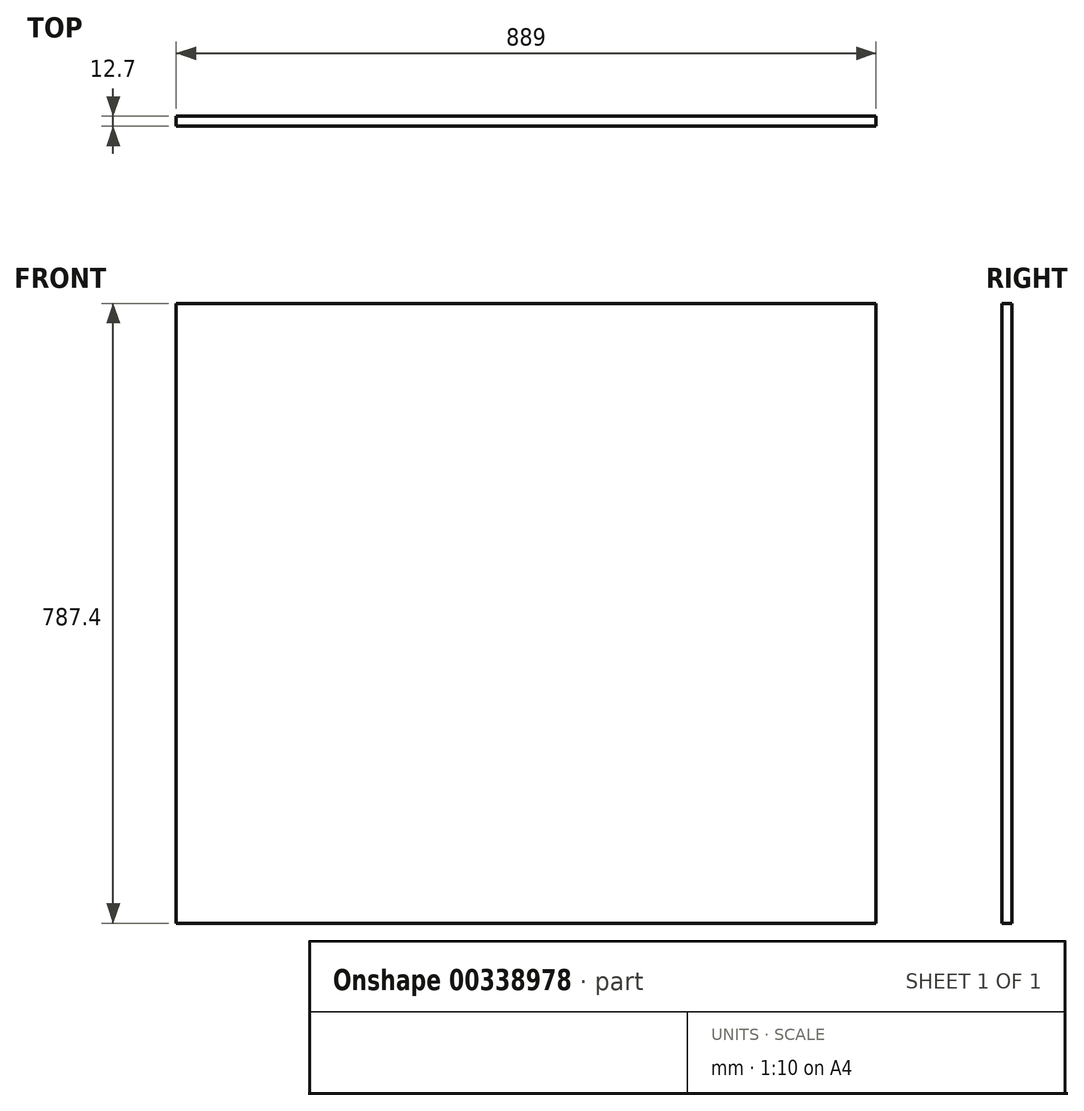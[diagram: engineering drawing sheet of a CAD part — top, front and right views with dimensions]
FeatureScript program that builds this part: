
annotation { "Feature Type Name" : "Feature", "Feature Type Description" : "" }
export const myFeature = defineFeature(function(context is Context, id is Id, definition is map)
    precondition{}
    {
        {
            var Q0;
            Q0=qCreatedBy(makeId("Front.planeOp"),FACE);
            var sketch = newSketch(context, id + "F0", { "sketchPlane" : qUnion([Q0])});
            skLineSegment(sketch, "E0.bottom", {"start": v(444.5, 393.7) * mm, "end": v(-444.5, 393.7) * mm});
            skLineSegment(sketch, "E0.top", {"start": v(444.5, -393.7) * mm, "end": v(-444.5, -393.7) * mm});
            skLineSegment(sketch, "E0.left", {"start": v(444.5, 393.7) * mm, "end": v(444.5, -393.7) * mm});
            skLineSegment(sketch, "E0.right", {"start": v(-444.5, 393.7) * mm, "end": v(-444.5, -393.7) * mm});
            skPoint(sketch, "E0.middle", {"position": v(0, 0) * mm});
            skSolve(sketch);
        }
        {
            var Q0;
            Q0 = qSketchRegion(id + "F0", true);
            extrude(context, id + "F1", {"entities" : qUnion([Q0]), "depth" : 12.7 * mm});
        }
    });
